# Revit family: TR
name_source: partatom
category: Mechanical Equipment
units: mm (PartAtom-declared; Revit-internal decimal feet)

## family parameters
Always vertical = Yes
Cut with Voids When Loaded = No
Part Type = Normal
Room Calculation Point = No
Round Connector Dimension = Use Diameter
Shared = No
Work Plane-Based = No

## types (9) — shared parameters
0 = 0' - 0"
1.5 = 0' - 1 1/2"
2" = 0' - 2"
Manufacturer = Loren Cook Company
Model = TR
ONE EIGTH = 0' - 0 1/8"
Type Comments = Spun Aluminum Tiered Intake/Relief Ventilator
URL = www.lorencook.com

## per-type parameters (varying)
| type | (C/2)-1.5" | 3 | A | A/2 | B | B/2 | C | D | G | G-.125" | RO | RO/2 | TSQ | TSQ/2 |
| 8-TR | 0' - 3 11/32" | 0' - 2 1/2" | 0' - 8 5/8" | 0' - 4 5/16" | 1' - 6 3/4" | 0' - 9 3/8" | 0' - 8 3/16" | 0' - 3 1/4" | 0' - 2" | 0' - 1 7/8" | 1' - 1 1/2" | 0' - 6 3/4" | 1' - 6" | 0' - 9" |
| 12-TR | 0' - 3 9/16" | 0' - 2 11/16" | 1' - 0 1/2" | 0' - 6 1/4" | 2' - 3 3/4" | 1' - 1 7/8" | 0' - 8 5/8" | 0' - 3 1/2" | 0' - 2" | 0' - 1 7/8" | 1' - 3 1/2" | 0' - 7 3/4" | 1' - 8" | 0' - 10" |
| 16-TR | 0' - 3 9/16" | 0' - 2 11/16" | 1' - 4 1/2" | 0' - 8 1/4" | 2' - 3 3/4" | 1' - 1 7/8" | 0' - 8 5/8" | 0' - 5 3/4" | 0' - 2" | 0' - 1 7/8" | 1' - 11 1/2" | 0' - 11 3/4" | 2' - 4" | 1' - 2" |
| 20-TR | 0' - 5 9/32" | 0' - 3 31/32" | 1' - 8 1/2" | 0' - 10 1/4" | 3' - 0 5/8" | 1' - 6 5/16" | 1' - 0 1/16" | 0' - 4 7/8" | 0' - 2" | 0' - 1 7/8" | 2' - 3 1/2" | 1' - 1 3/4" | 2' - 8" | 1' - 4" |
| 24-TR | 0' - 6 11/32" | 0' - 4 3/4" | 2' - 0 3/4" | 1' - 0 3/8" | 3' - 6 3/4" | 1' - 9 3/8" | 1' - 2 3/16" | 0' - 6 1/2" | 0' - 3" | 0' - 2 7/8" | 2' - 7 1/2" | 1' - 3 3/4" | 3' - 0" | 1' - 6" |
| 30-TR | 1' - 2 21/32" | 0' - 11" | 2' - 6 3/4" | 1' - 3 3/8" | 4' - 4 5/8" | 2' - 2 5/16" | 2' - 6 13/16" | 0' - 6 1/4" | 0' - 3" | 0' - 2 7/8" | 3' - 1 1/2" | 1' - 6 3/4" | 3' - 6" | 1' - 9" |
| 36-TR | 1' - 3 13/32" | 0' - 11 9/16" | 3' - 0 3/4" | 1' - 6 3/8" | 5' - 2 5/8" | 2' - 7 5/16" | 2' - 8 5/16" | 0' - 7 1/4" | 0' - 3" | 0' - 2 7/8" | 3' - 7 1/2" | 1' - 9 3/4" | 4' - 0" | 2' - 0" |
| 42-TR | 0' - 11 17/32" | 0' - 8 21/32" | 3' - 6 3/4" | 1' - 9 3/8" | 6' - 1 5/8" | 3' - 0 13/16" | 2' - 0 9/16" | 0' - 8 1/4" | 0' - 3" | 0' - 2 7/8" | 4' - 1 1/2" | 2' - 0 3/4" | 4' - 6" | 2' - 3" |
| 48-TR | 0' - 11 17/32" | 0' - 8 21/32" | 4' - 0 3/4" | 2' - 0 3/8" | 6' - 1 5/8" | 3' - 0 13/16" | 2' - 0 9/16" | 0' - 8 1/4" | 0' - 3" | 0' - 2 7/8" | 4' - 9 1/2" | 2' - 4 3/4" | 5' - 0" | 2' - 6" |

## geometry (parser evidence)
native form markers: Sweep x2
no freeform markers — native parametric forms only
